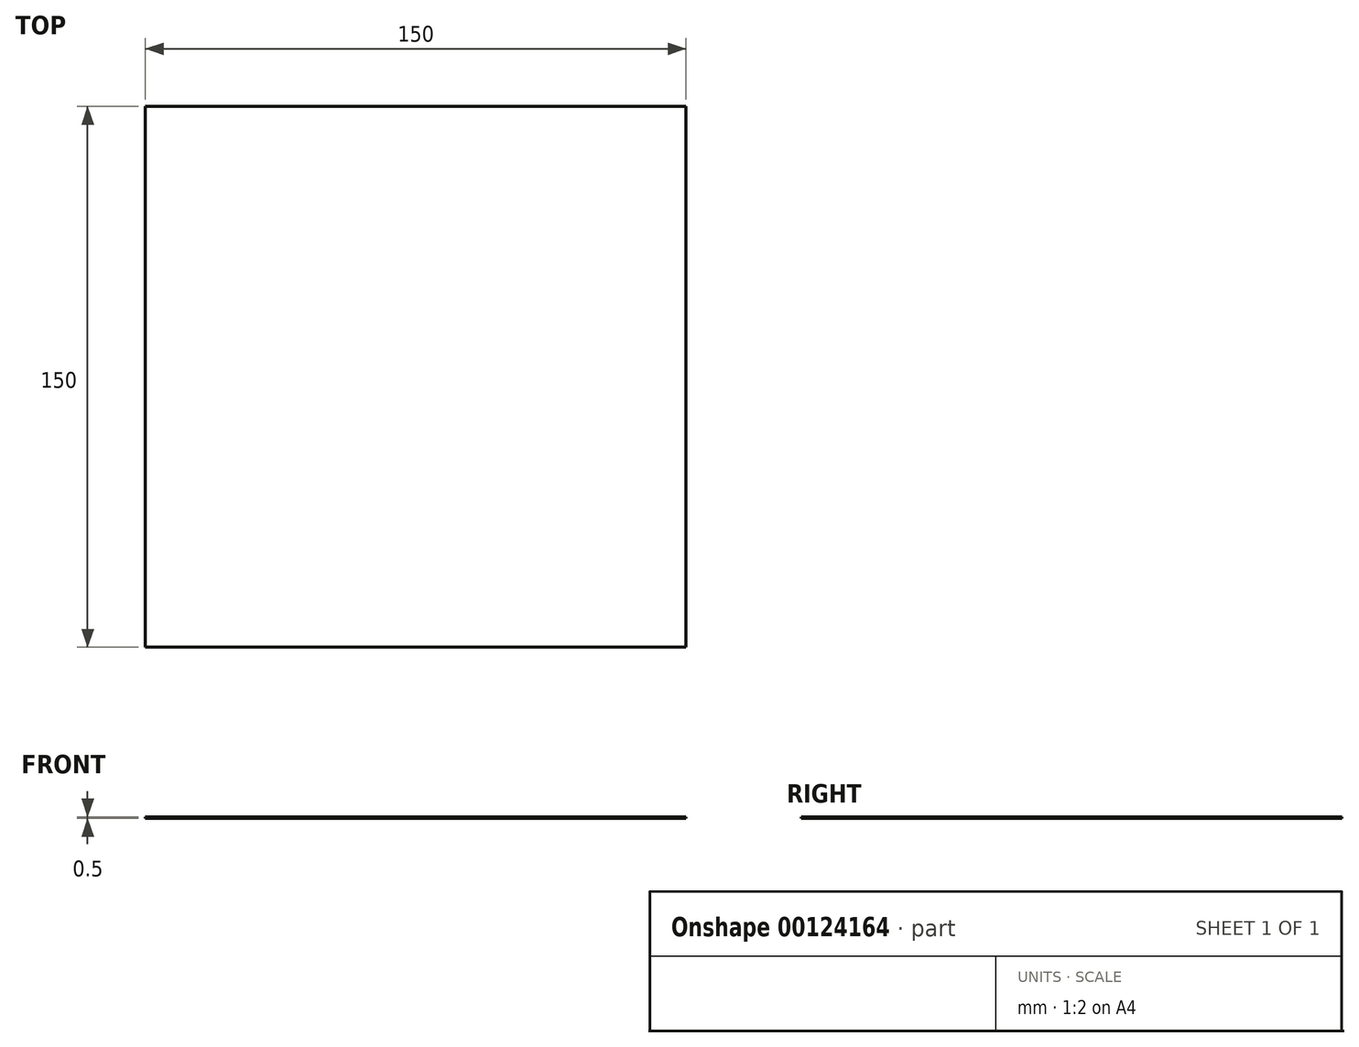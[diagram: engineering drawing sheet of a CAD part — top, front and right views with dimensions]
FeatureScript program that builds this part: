
annotation { "Feature Type Name" : "Feature", "Feature Type Description" : "" }
export const myFeature = defineFeature(function(context is Context, id is Id, definition is map)
    precondition{}
    {
        {
            var Q0;
            Q0=qCreatedBy(makeId("Top.planeOp"),FACE);
            var sketch = newSketch(context, id + "F0", { "sketchPlane" : qUnion([Q0])});
            skLineSegment(sketch, "E0.bottom", {"start": v(75, -75) * mm, "end": v(-75, -75) * mm});
            skLineSegment(sketch, "E0.top", {"start": v(75, 75) * mm, "end": v(-75, 75) * mm});
            skLineSegment(sketch, "E0.left", {"start": v(75, -75) * mm, "end": v(75, 75) * mm});
            skLineSegment(sketch, "E0.right", {"start": v(-75, -75) * mm, "end": v(-75, 75) * mm});
            skPoint(sketch, "E0.middle", {"position": v(0, 0) * mm});
            skSolve(sketch);
        }
        {
            var Q0;
            Q0=makeQuery(id+"F0.imprint","IMPRINT",FACE,{"disambiguationData":[TD([[makeQuery(id+"F0.imprint","IMPRINT",EDGE,{"derivedFrom":sQuery(id+"F0.wireOp",EDGE,"E0.bottom")}),-1.0]])]});
            extrude(context, id + "F1", {"entities" : qUnion([Q0]), "depth" : .5 * mm});
        }
    });
